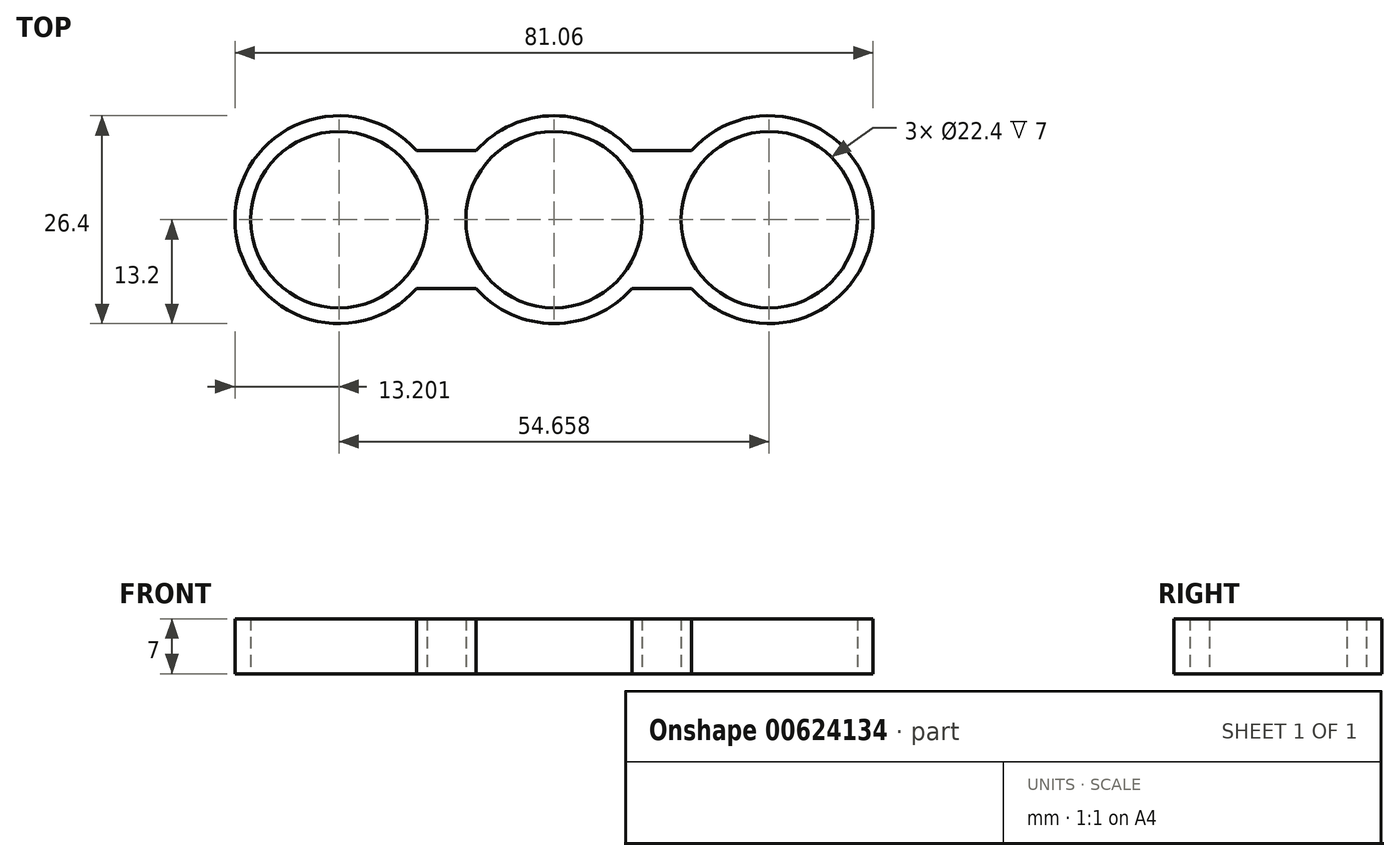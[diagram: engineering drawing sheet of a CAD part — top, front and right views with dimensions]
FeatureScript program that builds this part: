
annotation { "Feature Type Name" : "Feature", "Feature Type Description" : "" }
export const myFeature = defineFeature(function(context is Context, id is Id, definition is map)
    precondition{}
    {
        {
            var Q0;
            Q0=qCreatedBy(makeId("Top.planeOp"),FACE);
            var sketch = newSketch(context, id + "F0", { "sketchPlane" : qUnion([Q0])});
            skCircle(sketch, "E0", {"center": v(0, 0) * mm, "radius": 11.2 * mm});
            skCircle(sketch, "E1", {"center": v(-27.33, 0) * mm, "radius": 11.2 * mm});
            skCircle(sketch, "E2", {"center": v(0, 0) * mm, "radius": 13.2 * mm});
            skArc(sketch, "E3", {"start": v(-17.44, 8.75) * mm, "mid": v(-40.53, 0) * mm, "end": v(-17.44, -8.75) * mm});
            skArc(sketch, "E4.1.0", {"start": v(17.44, -8.75) * mm, "mid": v(40.53, 0) * mm, "end": v(17.44, 8.75) * mm});
            skCircle(sketch, "E4.1.1", {"center": v(27.33, 0) * mm, "radius": 11.2 * mm});
            skLineSegment(sketch, "E4.anchor1", {"start": v(0, 0) * mm, "end": v(-27.33, 0) * mm, "construction": true});
            skLineSegment(sketch, "E4.anchor2", {"start": v(0, 0) * mm, "end": v(27.33, 0) * mm, "construction": true});
            skLineSegment(sketch, "E5", {"start": v(-17.44, 8.75) * mm, "end": v(-9.89, 8.75) * mm});
            skLineSegment(sketch, "E6", {"start": v(17.44, 8.75) * mm, "end": v(9.89, 8.75) * mm});
            skLineSegment(sketch, "E7", {"start": v(-17.44, -8.75) * mm, "end": v(-9.89, -8.75) * mm});
            skLineSegment(sketch, "E8", {"start": v(9.89, -8.75) * mm, "end": v(17.44, -8.75) * mm});
            skSolve(sketch);
        }
        {
            var Q0;
            Q0=makeQuery(id+"F0.imprint","IMPRINT",FACE,{"disambiguationData":[TD([[makeQuery(id+"F0.imprint","IMPRINT",EDGE,{"derivedFrom":sQuery(id+"F0.wireOp",EDGE,"E1")}),-1.0]])]});
            var Q1;
            Q1=makeQuery(id+"F0.imprint","IMPRINT",FACE,{"disambiguationData":[TD([[makeQuery(id+"F0.imprint","IMPRINT",EDGE,{"derivedFrom":sQuery(id+"F0.wireOp",EDGE,"E4.1.0")}),1.0]])]});
            var Q2;
            Q2=makeQuery(id+"F0.imprint","IMPRINT",FACE,{"disambiguationData":[TD([[makeQuery(id+"F0.imprint","IMPRINT",EDGE,{"derivedFrom":sQuery(id+"F0.wireOp",EDGE,"E0")}),-1.0]])]});
            extrude(context, id + "F1", {"entities" : qUnion([Q0, Q1, Q2]), "depth" : 7 * mm, "offsetDistance" : 25 * mm});
        }
    });
